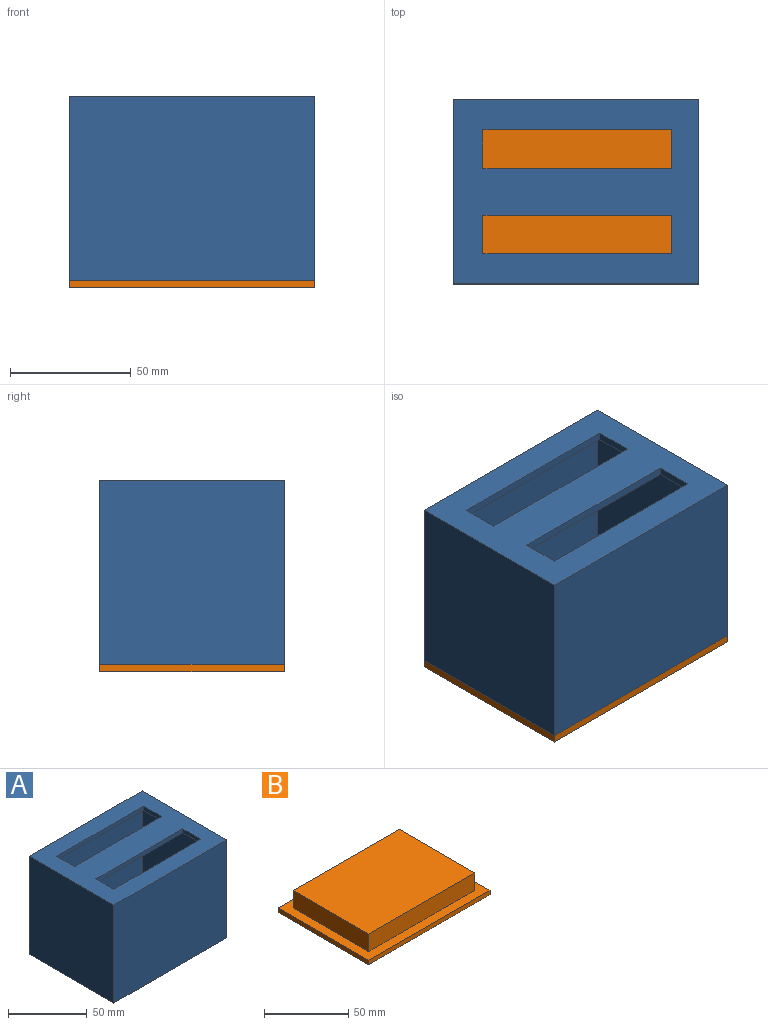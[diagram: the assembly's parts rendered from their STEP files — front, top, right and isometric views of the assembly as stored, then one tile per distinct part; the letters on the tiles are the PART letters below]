
ASSEMBLY  parts=2 mates=1
PART A: 19 faces, bbox 101.6x76.2x76.2 mm
  f0: plane 101.6x76.2mm, normal (0,0,1), area 5233.6mm2, adj f3,f4,f5,f6,f11,f12,f13,f14
  f1: plane 95.25x69.85mm, normal (0,0,-1), area 4144.9mm2, adj f7,f8,f9,f10,f11,f12,f13,f14
  f2: plane 101.6x76.2mm, normal (0,0,-1), area 1088.7mm2, adj f3,f4,f5,f6,f7,f8,f9,f10
  f3: plane 76.2x76.2mm, normal (-1,0,0), area 5806.4mm2, adj f0,f2,f4,f6
  f4: plane 101.6x76.2mm, normal (0,-1,0), area 7741.9mm2, adj f0,f2,f3,f5
  f5: plane 76.2x76.2mm, normal (1,0,0), area 5806.4mm2, adj f0,f2,f4,f6
  f6: plane 101.6x76.2mm, normal (0,1,0), area 7741.9mm2, adj f0,f2,f3,f5
  f7: plane 73.03x69.85mm, normal (1,0,0), area 5100.8mm2, adj f1,f2,f8,f10
  f8: plane 95.25x73.03mm, normal (0,1,0), area 6955.6mm2, adj f1,f2,f7,f9
  f9: plane 73.03x69.85mm, normal (-1,0,0), area 5100.8mm2, adj f1,f2,f8,f10
  f10: plane 95.25x73.03mm, normal (0,-1,0), area 6955.6mm2, adj f1,f2,f7,f9
  f11: plane 78.15x3.18mm, normal (0,-1,0), area 248.1mm2, adj f0,f1,f12,f14
  f12: plane 16.05x3.18mm, normal (1,0,0), area 51mm2, adj f0,f1,f11,f13
  f13: plane 78.15x3.18mm, normal (0,1,0), area 248.1mm2, adj f0,f1,f12,f14
  f14: plane 16.05x3.18mm, normal (-1,0,0), area 51mm2, adj f0,f1,f11,f13
  f15: plane 16.05x3.18mm, normal (1,0,0), area 51mm2, adj f0,f1,f16,f18
  f16: plane 78.15x3.18mm, normal (0,1,0), area 248.1mm2, adj f0,f1,f15,f17
  f17: plane 16.05x3.18mm, normal (-1,0,0), area 51mm2, adj f0,f1,f16,f18
  f18: plane 78.15x3.18mm, normal (0,-1,0), area 248.1mm2, adj f0,f1,f15,f17
PART B: 11 faces, bbox 101.6x76.2x15.9 mm
  f0: plane 101.6x76.2mm, normal (0,0,1), area 2096.8mm2, adj f1,f2,f3,f4,f6,f7,f8,f9
  f1: plane 76.2x3.18mm, normal (-1,0,0), area 241.9mm2, adj f0,f2,f4,f5
  f2: plane 101.6x3.18mm, normal (0,-1,0), area 322.6mm2, adj f0,f1,f3,f5
  f3: plane 76.2x3.18mm, normal (1,0,0), area 241.9mm2, adj f0,f2,f4,f5
  f4: plane 101.6x3.18mm, normal (0,1,0), area 322.6mm2, adj f0,f1,f3,f5
  f5: plane 101.6x76.2mm, normal (0,0,-1), area 7741.9mm2, adj f1,f2,f3,f4
  f6: plane 63.5x12.7mm, normal (-1,0,0), area 806.5mm2, adj f0,f7,f9,f10
  f7: plane 88.9x12.7mm, normal (0,-1,0), area 1129mm2, adj f0,f6,f8,f10
  f8: plane 63.5x12.7mm, normal (1,0,0), area 806.5mm2, adj f0,f7,f9,f10
  f9: plane 88.9x12.7mm, normal (0,1,0), area 1129mm2, adj f0,f6,f8,f10
  f10: plane 88.9x63.5mm, normal (0,0,1), area 5645.2mm2, adj f6,f7,f8,f9
PLACE A t=(-25.59,-13.93,-3.5)mm
PLACE B t=(-25.59,-13.93,-6.67)mm
MATE fastened A.f2 <-> B.f0  axis (0,0,-1) through (-25.59,-13.93,-3.5)mm
